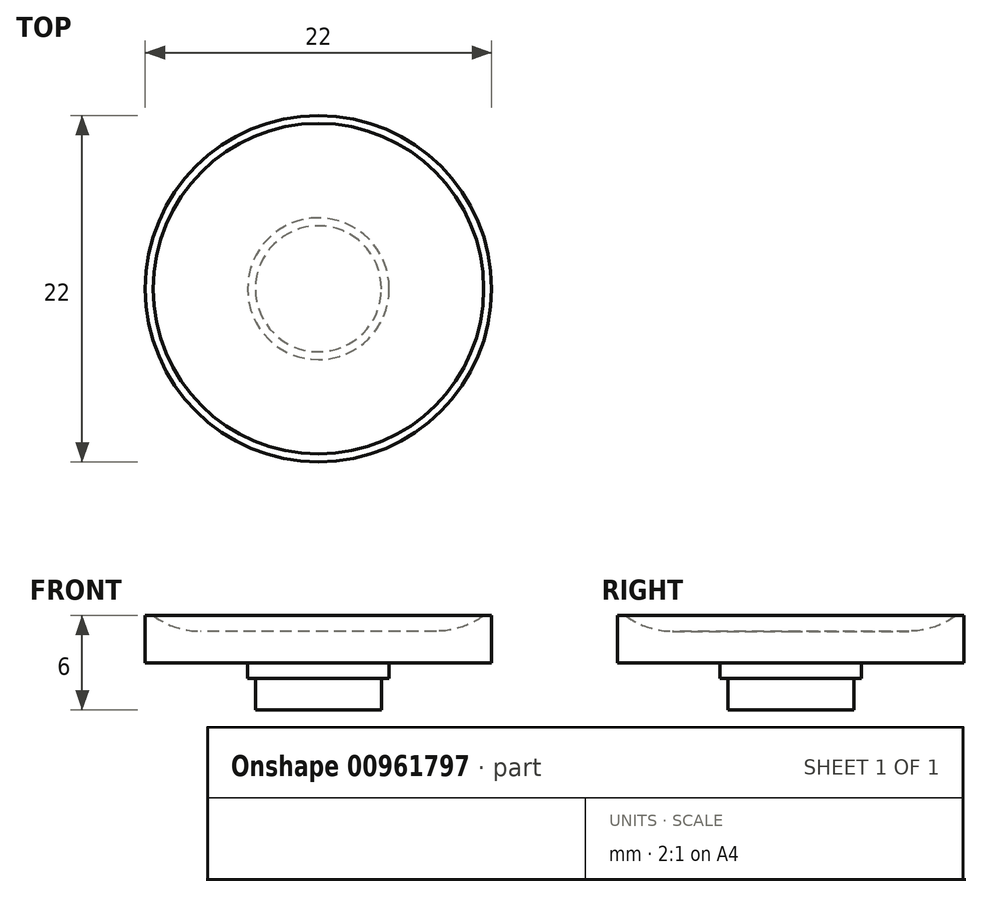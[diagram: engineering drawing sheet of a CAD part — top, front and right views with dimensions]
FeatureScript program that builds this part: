
annotation { "Feature Type Name" : "Feature", "Feature Type Description" : "" }
export const myFeature = defineFeature(function(context is Context, id is Id, definition is map)
    precondition{}
    {
        {
            var Q0;
            Q0=qCreatedBy(makeId("Top.planeOp"),FACE);
            var sketch = newSketch(context, id + "F0", { "sketchPlane" : qUnion([Q0])});
            skCircle(sketch, "E0", {"center": v(0, 0) * mm, "radius": 4 * mm});
            skCircle(sketch, "E1", {"center": v(0, 0) * mm, "radius": 4.5 * mm});
            skSolve(sketch);
        }
        {
            var Q0;
            Q0=makeQuery(id+"F0.imprint","IMPRINT",FACE,{"disambiguationData":[TD([[makeQuery(id+"F0.imprint","IMPRINT",EDGE,{"derivedFrom":sQuery(id+"F0.wireOp",EDGE,"E0")}),1.0]])]});
            extrude(context, id + "F1", {"entities" : qUnion([Q0]), "depth" : 0 * mm, "offsetDistance" : 25 * mm, "hasSecondDirection" : true, "secondDirectionOppositeDirection" : true, "secondDirectionDepth" : 2 * mm});
        }
        {
            var Q0;
            Q0=makeQuery(id+"F0.imprint","IMPRINT",FACE,{"disambiguationData":[TD([[makeQuery(id+"F0.imprint","IMPRINT",EDGE,{"derivedFrom":sQuery(id+"F0.wireOp",EDGE,"E0")}),-1.0]])]});
            var Q1;
            Q1=makeQuery(id+"F0.imprint","IMPRINT",FACE,{"disambiguationData":[TD([[makeQuery(id+"F0.imprint","IMPRINT",EDGE,{"derivedFrom":sQuery(id+"F0.wireOp",EDGE,"E0")}),1.0]])]});
            extrude(context, id + "F2", {"entities" : qUnion([Q0, Q1]), "operationType" : NewBodyOperationType.ADD, "depth" : 1 * mm, "offsetDistance" : 25 * mm});
        }
        {
            var Q0;
            Q0=makeQuery(id+"F2.opExtrude","CAP_FACE",FACE,{"disambiguationData":[OSD([sQuery(id+"F0.wireOp",EDGE,"E1")])],"isStart":false});
            var sketch = newSketch(context, id + "F3", { "sketchPlane" : qUnion([Q0])});
            skCircle(sketch, "E2", {"center": v(0, 0) * mm, "radius": 11 * mm});
            skSolve(sketch);
        }
        {
            var Q0;
            Q0 = qSketchRegion(id + "F3", true);
            extrude(context, id + "F4", {"entities" : qUnion([Q0]), "operationType" : NewBodyOperationType.ADD, "depth" : 3 * mm, "offsetDistance" : 25 * mm});
        }
        {
            var Q0;
            Q0=makeQuery(id+"F4.opExtrude","CAP_FACE",FACE,{"disambiguationData":[OSD([sQuery(id+"F3.wireOp",EDGE,"E2")])],"isStart":false});
            var sketch = newSketch(context, id + "F5", { "sketchPlane" : qUnion([Q0])});
            skCircle(sketch, "E3", {"center": v(0, 0) * mm, "radius": 10.5 * mm});
            skSolve(sketch);
        }
        {
            var Q0;
            Q0=makeQuery(id+"F5.imprint","IMPRINT",FACE,{"disambiguationData":[TD([[makeQuery(id+"F5.imprint","IMPRINT",EDGE,{"derivedFrom":sQuery(id+"F5.wireOp",EDGE,"E3")}),1.0]])]});
            extrude(context, id + "F6", {"entities" : qUnion([Q0]), "operationType" : NewBodyOperationType.REMOVE, "oppositeDirection" : true, "depth" : 1 * mm, "offsetDistance" : 25 * mm});
        }
        {
            var Q0;
            Q0=makeQuery(id+"F6.boolean.opBoolean","COPY",EDGE,{"derivedFrom":makeQuery(id+"F6.opExtrude","CAP_EDGE",EDGE,{"disambiguationData":[OSD([sQuery(id+"F5.wireOp",EDGE,"E3")])],"isStart":false})});
            fillet(context, id + "F7", {"entities" : qUnion([Q0]), "radius" : 5 * mm, "tangentPropagation" : true, "allowEdgeOverflow" : false});
        }
    });
